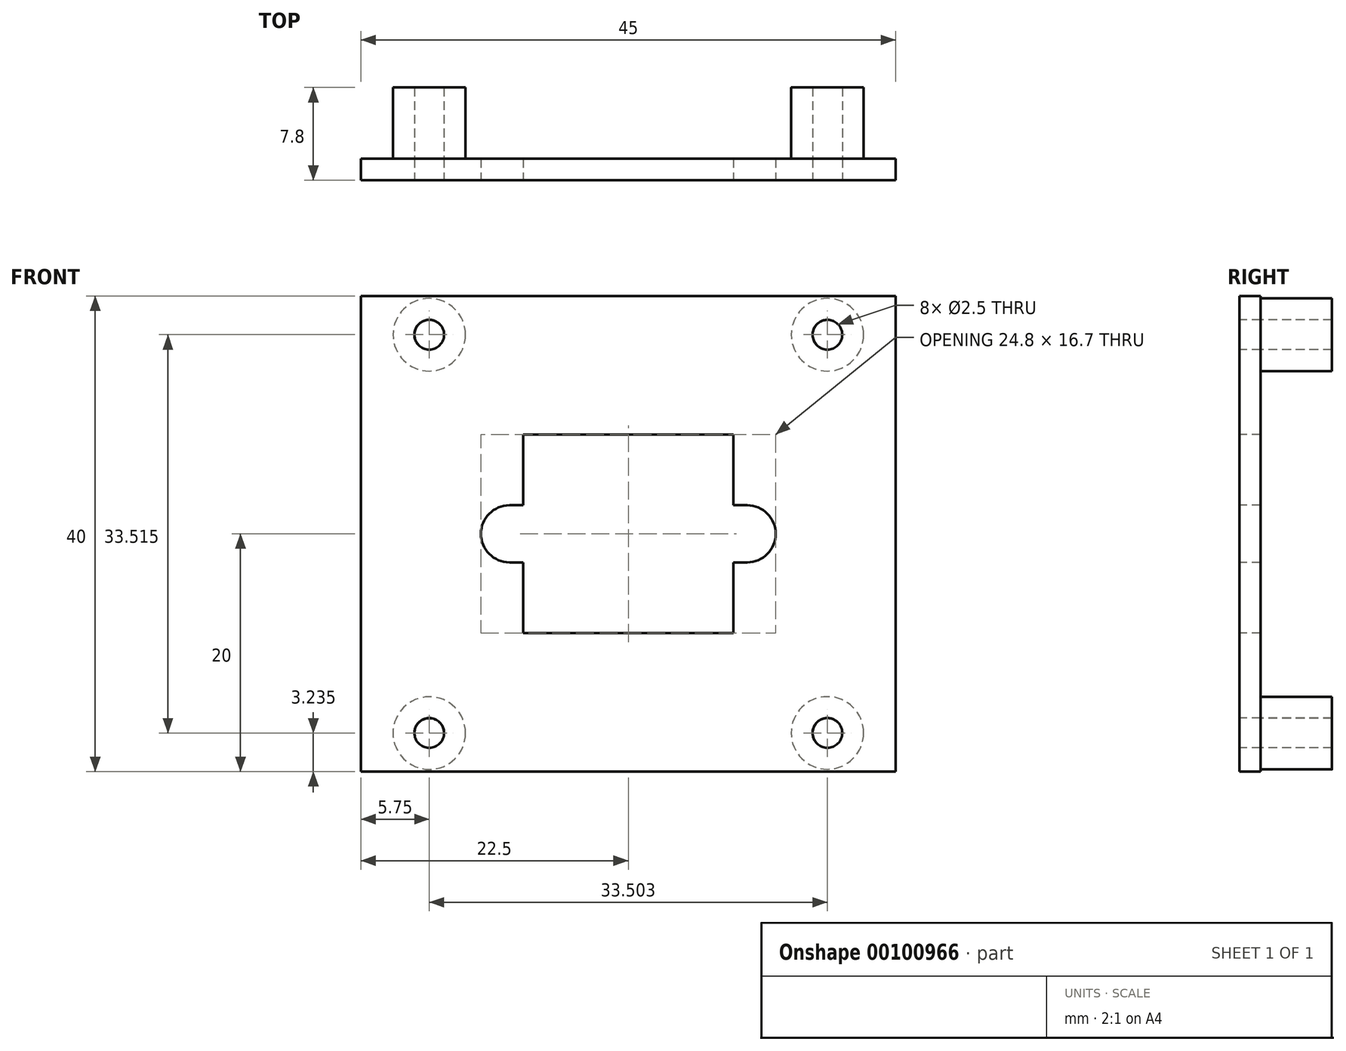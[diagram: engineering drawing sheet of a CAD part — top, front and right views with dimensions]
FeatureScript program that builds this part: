
annotation { "Feature Type Name" : "Feature", "Feature Type Description" : "" }
export const myFeature = defineFeature(function(context is Context, id is Id, definition is map)
    precondition{}
    {
        {
            var Q0;
            Q0=qCreatedBy(makeId("Front.planeOp"),FACE);
            var sketch = newSketch(context, id + "F0", { "sketchPlane" : qUnion([Q0])});
            skLineSegment(sketch, "E0.bottom", {"start": v(-8.85, 8.35) * mm, "end": v(8.85, 8.35) * mm});
            skLineSegment(sketch, "E0.top", {"start": v(-8.85, -8.35) * mm, "end": v(8.85, -8.35) * mm});
            skLineSegment(sketch, "E0.left", {"start": v(-8.85, 8.35) * mm, "end": v(-8.85, -8.35) * mm});
            skLineSegment(sketch, "E0.right", {"start": v(8.85, 8.35) * mm, "end": v(8.85, -8.35) * mm});
            skPoint(sketch, "E0.middle", {"position": v(0, 0) * mm});
            skLineSegment(sketch, "E1.bottom", {"start": v(-8.85, 2.4) * mm, "end": v(-10, 2.4) * mm});
            skLineSegment(sketch, "E1.top", {"start": v(-8.85, -2.4) * mm, "end": v(-10, -2.4) * mm});
            skLineSegment(sketch, "E1.left", {"start": v(-8.85, 2.4) * mm, "end": v(-8.85, -2.4) * mm});
            skLineSegment(sketch, "E1.right", {"start": v(-10, 2.4) * mm, "end": v(-10, -2.4) * mm});
            skPoint(sketch, "E2.oppositeSnap0", {"position": v(-9.42, 2.4) * mm});
            skLineSegment(sketch, "E2.bottom", {"start": v(8.85, -2.4) * mm, "end": v(10, -2.4) * mm});
            skLineSegment(sketch, "E2.top", {"start": v(8.85, 2.4) * mm, "end": v(10, 2.4) * mm});
            skLineSegment(sketch, "E2.left", {"start": v(8.85, -2.4) * mm, "end": v(8.85, 2.4) * mm});
            skLineSegment(sketch, "E2.right", {"start": v(10, -2.4) * mm, "end": v(10, 2.4) * mm});
            skArc(sketch, "E3", {"start": v(-10, 2.4) * mm, "mid": v(-12.4, 0) * mm, "end": v(-10, -2.4) * mm});
            skArc(sketch, "E4", {"start": v(10, 2.4) * mm, "mid": v(12.4, 0) * mm, "end": v(10, -2.4) * mm});
            skCircle(sketch, "E5", {"center": v(-16.75, 16.75) * mm, "radius": 1.05 * mm});
            skCircle(sketch, "E6", {"center": v(16.75, -16.75) * mm, "radius": 1.25 * mm});
            skCircle(sketch, "E7", {"center": v(-16.75, 16.75) * mm, "radius": 1.25 * mm});
            skCircle(sketch, "E8", {"center": v(16.75, 16.75) * mm, "radius": 1.25 * mm});
            skCircle(sketch, "E9", {"center": v(-16.75, -16.75) * mm, "radius": 1.25 * mm});
            skSolve(sketch);
        }
        {
            var Q0;
            Q0=qCreatedBy(makeId("Front.planeOp"),FACE);
            var sketch = newSketch(context, id + "F1", { "sketchPlane" : qUnion([Q0])});
            skLineSegment(sketch, "E10.bottom", {"start": v(22.5, -20) * mm, "end": v(-22.5, -20) * mm});
            skLineSegment(sketch, "E10.top", {"start": v(22.5, 20) * mm, "end": v(-22.5, 20) * mm});
            skLineSegment(sketch, "E10.left", {"start": v(22.5, -20) * mm, "end": v(22.5, 20) * mm});
            skLineSegment(sketch, "E10.right", {"start": v(-22.5, -20) * mm, "end": v(-22.5, 20) * mm});
            skPoint(sketch, "E10.middle", {"position": v(0, 0) * mm});
            skSolve(sketch);
        }
        {
            var Q0;
            Q0 = qSketchRegion(id + "F1", true);
            extrude(context, id + "F2", {"entities" : qUnion([Q0]), "oppositeDirection" : true, "depth" : 1.8 * mm});
        }
        {
            var Q0;
            Q0 = qSketchRegion(id + "F0", true);
            var Q1;
            Q1=makeQuery(id+"F0.imprint","IMPRINT",FACE,{"disambiguationData":[TD([[makeQuery(id+"F0.imprint","IMPRINT",EDGE,{"derivedFrom":sQuery(id+"F0.wireOp",EDGE,"E5")}),1.0]])]});
            extrude(context, id + "F3", {"entities" : qUnion([Q0, Q1]), "operationType" : NewBodyOperationType.REMOVE, "oppositeDirection" : true, "depth" : 1.8 * mm});
        }
        {
            var Q0;
            {var subQ6=sQuery(id+"F1.wireOp",EDGE,"E10.left");var subQ10=sQuery(id+"F1.wireOp",EDGE,"E10.bottom");var subQ11=sQuery(id+"F1.wireOp",EDGE,"E10.right");var subQ12=sQuery(id+"F1.wireOp",EDGE,"E10.top");Q0=makeQuery(id+"F3.boolean.opBoolean","SPLIT",FACE,{"disambiguationData":[TD([makeQuery(id+"F2.opExtrude","SWEPT_FACE",FACE,{"disambiguationData":[OSD([subQ10])]})])],"derivedFrom":makeQuery(id+"F2.opExtrude","CAP_FACE",FACE,{"disambiguationData":[OSD([subQ10,subQ12,subQ6,subQ11])],"isStart":false})});}
            var sketch = newSketch(context, id + "F4", { "sketchPlane" : qUnion([Q0])});
            skCircle(sketch, "E11", {"center": v(-16.75, -16.75) * mm, "radius": 1.25 * mm});
            skCircle(sketch, "E12", {"center": v(16.75, 16.75) * mm, "radius": 1.25 * mm});
            skCircle(sketch, "E13.0", {"center": v(16.75, 16.75) * mm, "radius": 3.05 * mm});
            skCircle(sketch, "E14.0", {"center": v(-16.75, -16.75) * mm, "radius": 3.05 * mm});
            skCircle(sketch, "E15", {"center": v(-16.75, 16.75) * mm, "radius": 1.25 * mm});
            skCircle(sketch, "E16.0", {"center": v(-16.75, 16.75) * mm, "radius": 3.05 * mm});
            skCircle(sketch, "E17", {"center": v(16.75, -16.77) * mm, "radius": 1.25 * mm});
            skCircle(sketch, "E18.0", {"center": v(16.75, -16.77) * mm, "radius": 3.05 * mm});
            skSolve(sketch);
        }
        {
            var Q0;
            Q0 = qSketchRegion(id + "F4", true);
            extrude(context, id + "F5", {"entities" : qUnion([Q0]), "depth" : 6 * mm});
        }
    });
